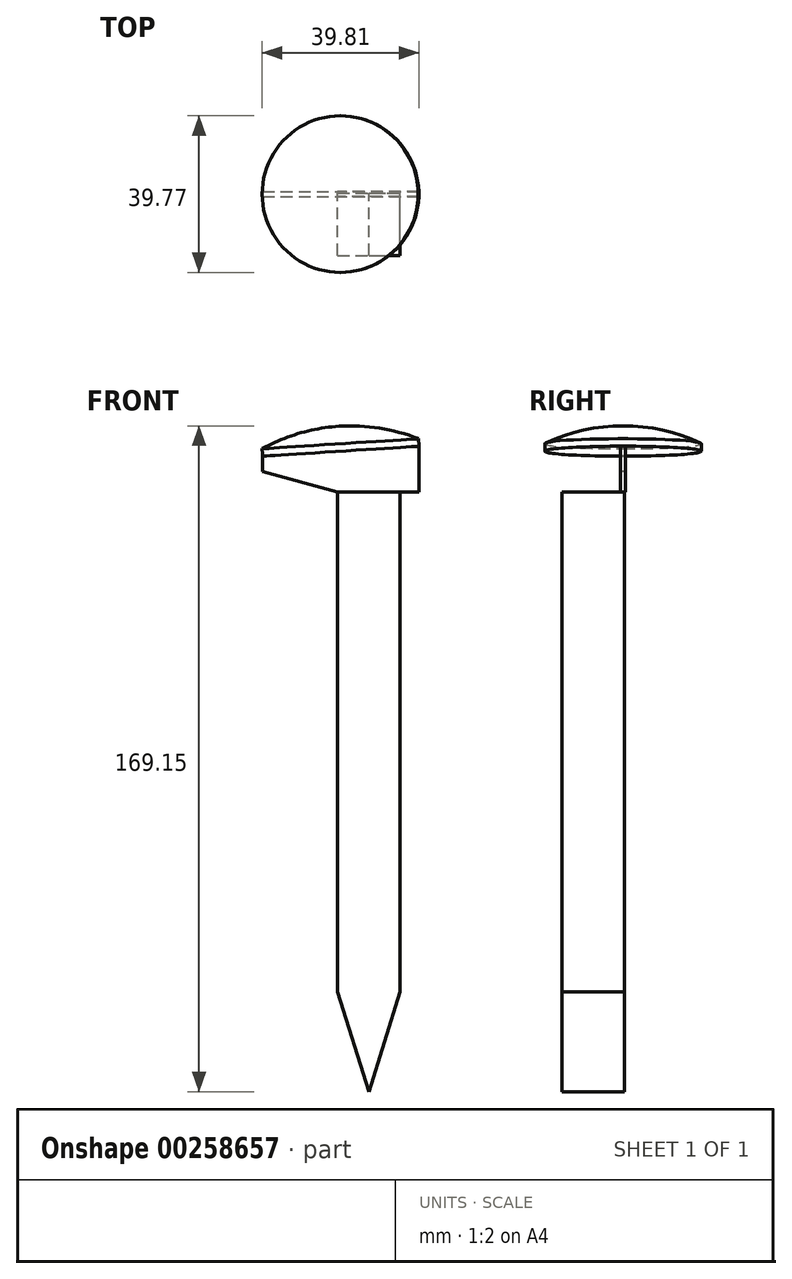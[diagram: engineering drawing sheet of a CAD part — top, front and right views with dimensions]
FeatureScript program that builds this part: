
annotation { "Feature Type Name" : "Feature", "Feature Type Description" : "" }
export const myFeature = defineFeature(function(context is Context, id is Id, definition is map)
    precondition{}
    {
        {
            var Q0;
            Q0=qCreatedBy(makeId("Front.planeOp"),FACE);
            var sketch = newSketch(context, id + "F0", { "sketchPlane" : qUnion([Q0])});
            skLineSegment(sketch, "E0.bottom", {"start": v(0, 0) * mm, "end": v(15.88, 0) * mm, "construction": true});
            skLineSegment(sketch, "E0.top", {"start": v(0, 152.4) * mm, "end": v(15.87, 152.4) * mm});
            skLineSegment(sketch, "E0.left", {"start": v(0, 0) * mm, "end": v(0, 152.4) * mm, "construction": true});
            skLineSegment(sketch, "E0.right", {"start": v(15.88, 0) * mm, "end": v(15.87, 152.4) * mm, "construction": true});
            skLineSegment(sketch, "E1", {"start": v(0, 25.4) * mm, "end": v(7.94, 0) * mm});
            skLineSegment(sketch, "E2", {"start": v(7.94, 0) * mm, "end": v(15.88, 25.4) * mm});
            skLineSegment(sketch, "E3", {"start": v(0, 152.4) * mm, "end": v(0, 25.4) * mm});
            skLineSegment(sketch, "E4", {"start": v(15.88, 25.4) * mm, "end": v(15.87, 152.4) * mm});
            skSolve(sketch);
        }
        {
            var Q0;
            Q0 = qSketchRegion(id + "F0", true);
            extrude(context, id + "F1", {"entities" : qUnion([Q0]), "depth" : 15.88 * mm});
        }
        {
            var Q0;
            Q0=qCreatedBy(makeId("Front.planeOp"),FACE);
            var sketch = newSketch(context, id + "F2", { "sketchPlane" : qUnion([Q0])});
            skLineSegment(sketch, "E5.bottom", {"start": v(20.64, 152.4) * mm, "end": v(-19.05, 152.4) * mm});
            skLineSegment(sketch, "E5.top", {"start": v(20.64, 169.07) * mm, "end": v(-19.05, 169.07) * mm});
            skLineSegment(sketch, "E5.left", {"start": v(20.64, 152.4) * mm, "end": v(20.64, 169.07) * mm});
            skLineSegment(sketch, "E5.right", {"start": v(-19.05, 152.4) * mm, "end": v(-19.05, 169.07) * mm});
            skSolve(sketch);
        }
        {
            var Q0;
            Q0 = qSketchRegion(id + "F2", true);
            extrude(context, id + "F3", {"entities" : qUnion([Q0]), "operationType" : NewBodyOperationType.ADD, "depth" : (5 / 8 + ((1 + 5 / 16 - 5 / 8) / 2)) * mm, "hasSecondDirection" : true, "secondDirectionOppositeDirection" : true, "secondDirectionDepth" : ((1 + 5 / 16 - 5 / 8) / 2) * mm});
        }
        {
            var Q0;
            Q0=makeQuery(id+"F3.opExtrude","CAP_FACE",FACE,{"disambiguationData":[OSD([sQuery(id+"F2.wireOp",EDGE,"E5.bottom"),sQuery(id+"F2.wireOp",EDGE,"E5.top"),sQuery(id+"F2.wireOp",EDGE,"E5.left"),sQuery(id+"F2.wireOp",EDGE,"E5.right")])],"isStart":false});
            var sketch = newSketch(context, id + "F4", { "sketchPlane" : qUnion([Q0])});
            skLineSegment(sketch, "E6", {"start": v(-19.05, 157.5) * mm, "end": v(0, 152.4) * mm});
            skLineSegment(sketch, "E7", {"start": v(-19.05, 157.5) * mm, "end": v(20.64, 157.5) * mm, "construction": true});
            skLineSegment(sketch, "E8", {"start": v(-19.05, 157.5) * mm, "end": v(-19.05, 152.4) * mm});
            skLineSegment(sketch, "E9", {"start": v(-19.05, 152.4) * mm, "end": v(0, 152.4) * mm});
            skSolve(sketch);
        }
        {
            var Q0;
            Q0 = qSketchRegion(id + "F4", true);
            extrude(context, id + "F5", {"entities" : qUnion([Q0]), "operationType" : NewBodyOperationType.REMOVE, "endBound" : BoundingType.THROUGH_ALL, "oppositeDirection" : true, "depth" : 25.4 * mm});
        }
        {
            var Q0;
            Q0=makeQuery(id+"F3.opExtrude","CAP_FACE",FACE,{"disambiguationData":[OSD([sQuery(id+"F2.wireOp",EDGE,"E5.bottom"),sQuery(id+"F2.wireOp",EDGE,"E5.top"),sQuery(id+"F2.wireOp",EDGE,"E5.left"),sQuery(id+"F2.wireOp",EDGE,"E5.right")])],"isStart":false});
            var sketch = newSketch(context, id + "F6", { "sketchPlane" : qUnion([Q0])});
            skLineSegment(sketch, "E10", {"start": v(-19.05, 161.45) * mm, "end": v(20.64, 163.99) * mm});
            skLineSegment(sketch, "E11", {"start": v(20.64, 163.99) * mm, "end": v(20.64, 169.07) * mm});
            skLineSegment(sketch, "E12", {"start": v(20.64, 169.07) * mm, "end": v(-19.05, 169.07) * mm});
            skLineSegment(sketch, "E13", {"start": v(-19.05, 169.07) * mm, "end": v(-19.05, 161.45) * mm});
            skSolve(sketch);
        }
        {
            var Q0;
            Q0 = qSketchRegion(id + "F6", true);
            extrude(context, id + "F7", {"entities" : qUnion([Q0]), "operationType" : NewBodyOperationType.REMOVE, "endBound" : BoundingType.THROUGH_ALL, "oppositeDirection" : true, "depth" : 25.4 * mm});
        }
        {
            var Q0;
            Q0=makeQuery(id+"F3.opExtrude","CAP_FACE",FACE,{"disambiguationData":[OSD([sQuery(id+"F2.wireOp",EDGE,"E5.bottom"),sQuery(id+"F2.wireOp",EDGE,"E5.top"),sQuery(id+"F2.wireOp",EDGE,"E5.left"),sQuery(id+"F2.wireOp",EDGE,"E5.right")])],"isStart":false});
            var Q1;
            Q1=makeQuery(id+"F3.opExtrude","CAP_FACE",FACE,{"disambiguationData":[OSD([sQuery(id+"F2.wireOp",EDGE,"E5.bottom"),sQuery(id+"F2.wireOp",EDGE,"E5.top"),sQuery(id+"F2.wireOp",EDGE,"E5.left"),sQuery(id+"F2.wireOp",EDGE,"E5.right")])],"isStart":true});
            cPlane(context, id + "F8", {"entities" : qUnion([Q0, Q1]), "cplaneType" : CPlaneType.MID_PLANE, "offset" : 25.4 * mm, "width" : 152.4 * mm, "height" : 152.4 * mm});
        }
        {
            var Q0;
            Q0=qCreatedBy(id+"F8.planeOp",FACE);
            var sketch = newSketch(context, id + "F9", { "sketchPlane" : qUnion([Q0])});
            skLineSegment(sketch, "E14", {"start": v(20.64, 163.99) * mm, "end": v(-19.05, 161.45) * mm, "construction": true});
            skLineSegment(sketch, "E15", {"start": v(-19.05, 161.45) * mm, "end": v(-19.17, 163.35) * mm});
            skLineSegment(sketch, "E16", {"start": v(20.64, 163.99) * mm, "end": v(20.52, 165.89) * mm, "construction": true});
            skLineSegment(sketch, "E17", {"start": v(20.52, 165.89) * mm, "end": v(-19.17, 163.35) * mm, "construction": true});
            skArc(sketch, "E18", {"start": v(0.39, 169.06) * mm, "mid": v(-9.7, 167.28) * mm, "end": v(-19.17, 163.35) * mm});
            skLineSegment(sketch, "E19", {"start": v(0.8, 162.72) * mm, "end": v(0.39, 169.06) * mm});
            skLineSegment(sketch, "E20", {"start": v(-19.05, 161.45) * mm, "end": v(0.8, 162.72) * mm});
            skSolve(sketch);
        }
        {
            var Q0;
            Q0 = qSketchRegion(id + "F9", true);
            var Q1;
            Q1=sQuery(id+"F9.wireOp",EDGE,"E19");
            revolve(context, id + "F10", {"operationType" : NewBodyOperationType.ADD, "entities" : qUnion([Q0]), "axis" : qUnion([Q1]), "revolveType" : RevolveType.FULL});
        }
    });
